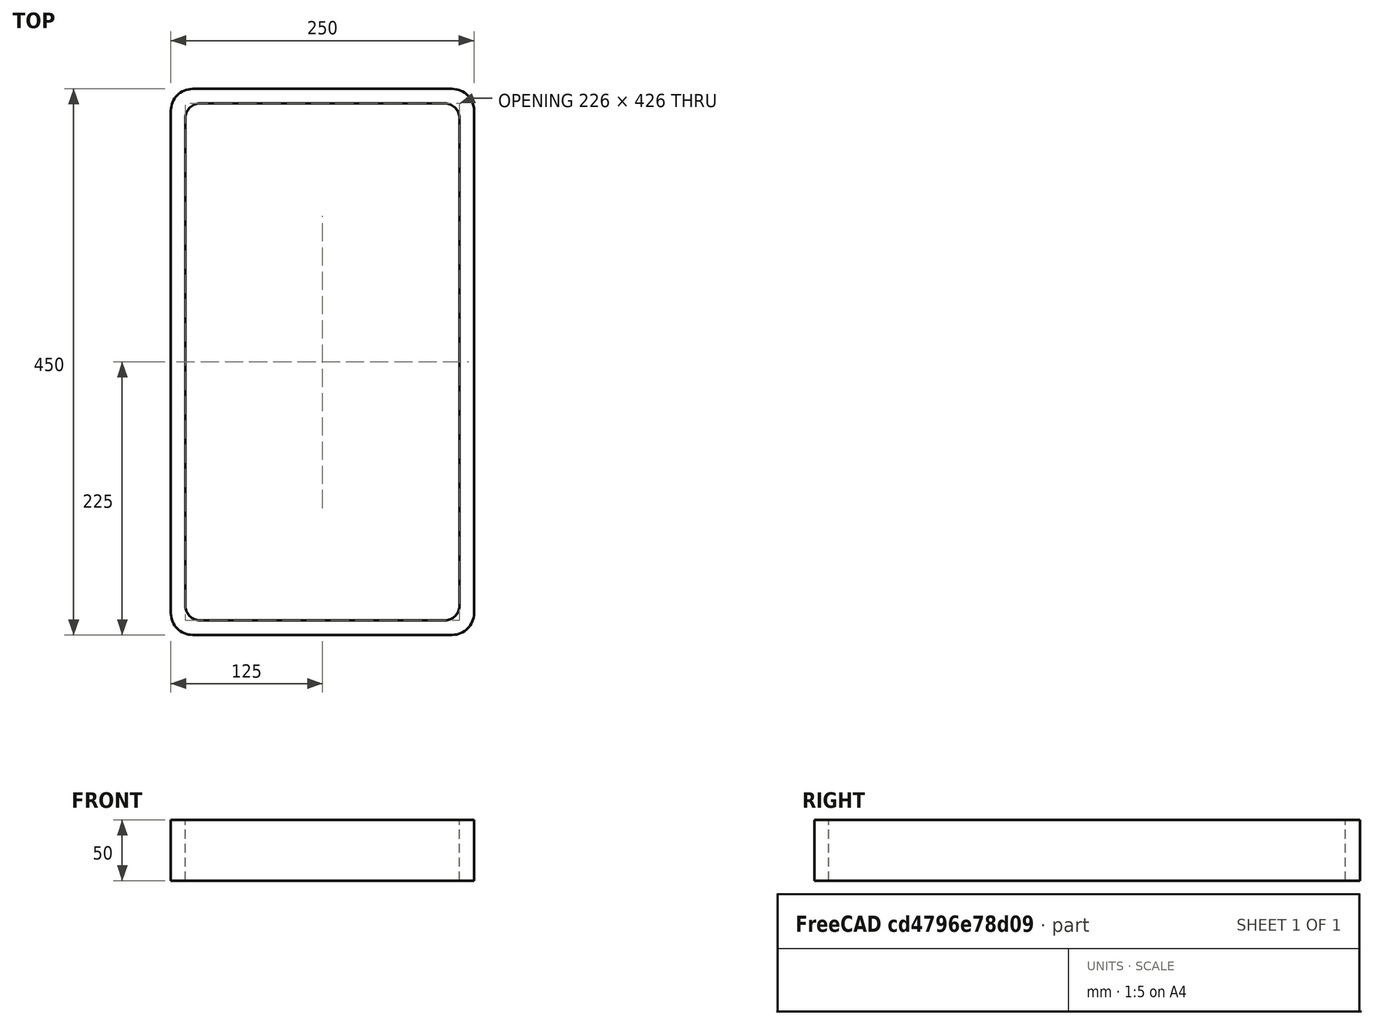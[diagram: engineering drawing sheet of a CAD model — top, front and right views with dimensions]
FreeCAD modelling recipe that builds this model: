
FCSTD DOCUMENT  (FreeCAD 0.15R4671 (Git))
Label: Rectangular hollow section 450x250x12 EN10219 S235JRH
License: All rights reserved
LicenseURL: http://en.wikipedia.org/wiki/All_rights_reserved
objects: Sketcher::SketchObject×1, Part::Extrusion×1
note: 2 computed .brp shape members not serialized (recipe doc carries the construction recipe); baked Part::Feature solids carry a one-line shape summary decoded from their .brp

FEATURE [Sketcher::SketchObject] Sketch
  sketch-geometry (16):
    g0: LineSegment StartX=-101 StartY=213 StartZ=0 EndX=101 EndY=213 EndZ=0
    g1: LineSegment StartX=113 StartY=201 StartZ=0 EndX=113 EndY=-201 EndZ=0
    g2: LineSegment StartX=101 StartY=-213 StartZ=0 EndX=-101 EndY=-213 EndZ=0
    g3: LineSegment StartX=-113 StartY=-201 StartZ=0 EndX=-113 EndY=201 EndZ=0
    g4: LineSegment StartX=-107 StartY=225 StartZ=0 EndX=107 EndY=225 EndZ=0
    g5: LineSegment StartX=125 StartY=207 StartZ=0 EndX=125 EndY=-207 EndZ=0
    g6: LineSegment StartX=107 StartY=-225 StartZ=0 EndX=-107 EndY=-225 EndZ=0
    g7: LineSegment StartX=-125 StartY=-207 StartZ=0 EndX=-125 EndY=207 EndZ=0
    g8: ArcOfCircle CenterX=-101 CenterY=201 CenterZ=0 NormalX=0 NormalY=0 NormalZ=1 Radius=12 StartAngle=1.5708 EndAngle=3.14159
    g9: ArcOfCircle CenterX=101 CenterY=201 CenterZ=0 NormalX=0 NormalY=0 NormalZ=1 Radius=12 StartAngle=0 EndAngle=1.5708
    g10: ArcOfCircle CenterX=101 CenterY=-201 CenterZ=0 NormalX=0 NormalY=0 NormalZ=1 Radius=12 StartAngle=4.71239 EndAngle=6.28319
    g11: ArcOfCircle CenterX=-101 CenterY=-201 CenterZ=0 NormalX=0 NormalY=0 NormalZ=1 Radius=12 StartAngle=3.14159 EndAngle=4.71239
    g12: ArcOfCircle CenterX=107 CenterY=207 CenterZ=0 NormalX=0 NormalY=0 NormalZ=1 Radius=18 StartAngle=0 EndAngle=1.5708
    g13: ArcOfCircle CenterX=107 CenterY=-207 CenterZ=0 NormalX=0 NormalY=0 NormalZ=1 Radius=18 StartAngle=4.71239 EndAngle=6.28319
    g14: ArcOfCircle CenterX=-107 CenterY=-207 CenterZ=0 NormalX=0 NormalY=0 NormalZ=1 Radius=18 StartAngle=3.14159 EndAngle=4.71239
    g15: ArcOfCircle CenterX=-107 CenterY=207 CenterZ=0 NormalX=0 NormalY=0 NormalZ=1 Radius=18 StartAngle=1.5708 EndAngle=3.14159
  constraints (36):
    c: Horizontal(g2)
    c: Vertical(g3)
    c: Horizontal(g6)
    c: Vertical(g7)
    c: Tangent(g3,g8) = 1.5708
    c: Tangent(g0,g8) = 1.5708
    c: Tangent(g0,g9) = 1.5708
    c: Tangent(g1,g9) = 1.5708
    c: Tangent(g1,g10) = 1.5708
    c: Tangent(g2,g10) = 1.5708
    c: Tangent(g2,g11) = 1.5708
    c: Tangent(g3,g11) = 1.5708
    c: Tangent(g4,g12) = 1.5708
    c: Tangent(g5,g12) = 1.5708
    c: Tangent(g5,g13) = 1.5708
    c: Tangent(g6,g13) = 1.5708
    c: Tangent(g6,g14) = 1.5708
    c: Tangent(g7,g14) = 1.5708
    c: Tangent(g7,g15) = 1.5708
    c: Tangent(g4,g15) = 1.5708
    c: Equal(g9,g8)
    c: Equal(g9,g11)
    c: Equal(g9,g10)
    c: Equal(g12,g15)
    c: Equal(g12,g14)
    c: Equal(g12,g13)
    c: Symmetric(g4,g6,g-1)
    c: Symmetric(g7,g5,g-2)
    c: DistanceY(g4,g6) = -450
    c: DistanceX(g7,g5) = 250
    c: Symmetric(g3,g1,g-2)
    c: Symmetric(g0,g2,g-1)
    c: DistanceY(g0,g4) = 12
    c: DistanceX(g5,g1) = -12
    c: Radius(g9) = 12
    c: Radius(g12) = 18
FEATURE [Part::Extrusion] Extrude  label="Rectangular hollow section 450x250x12 EN10219 S235JRH"
  Base = -> Sketch
  Dir = (0,0,50)
  Solid = true
